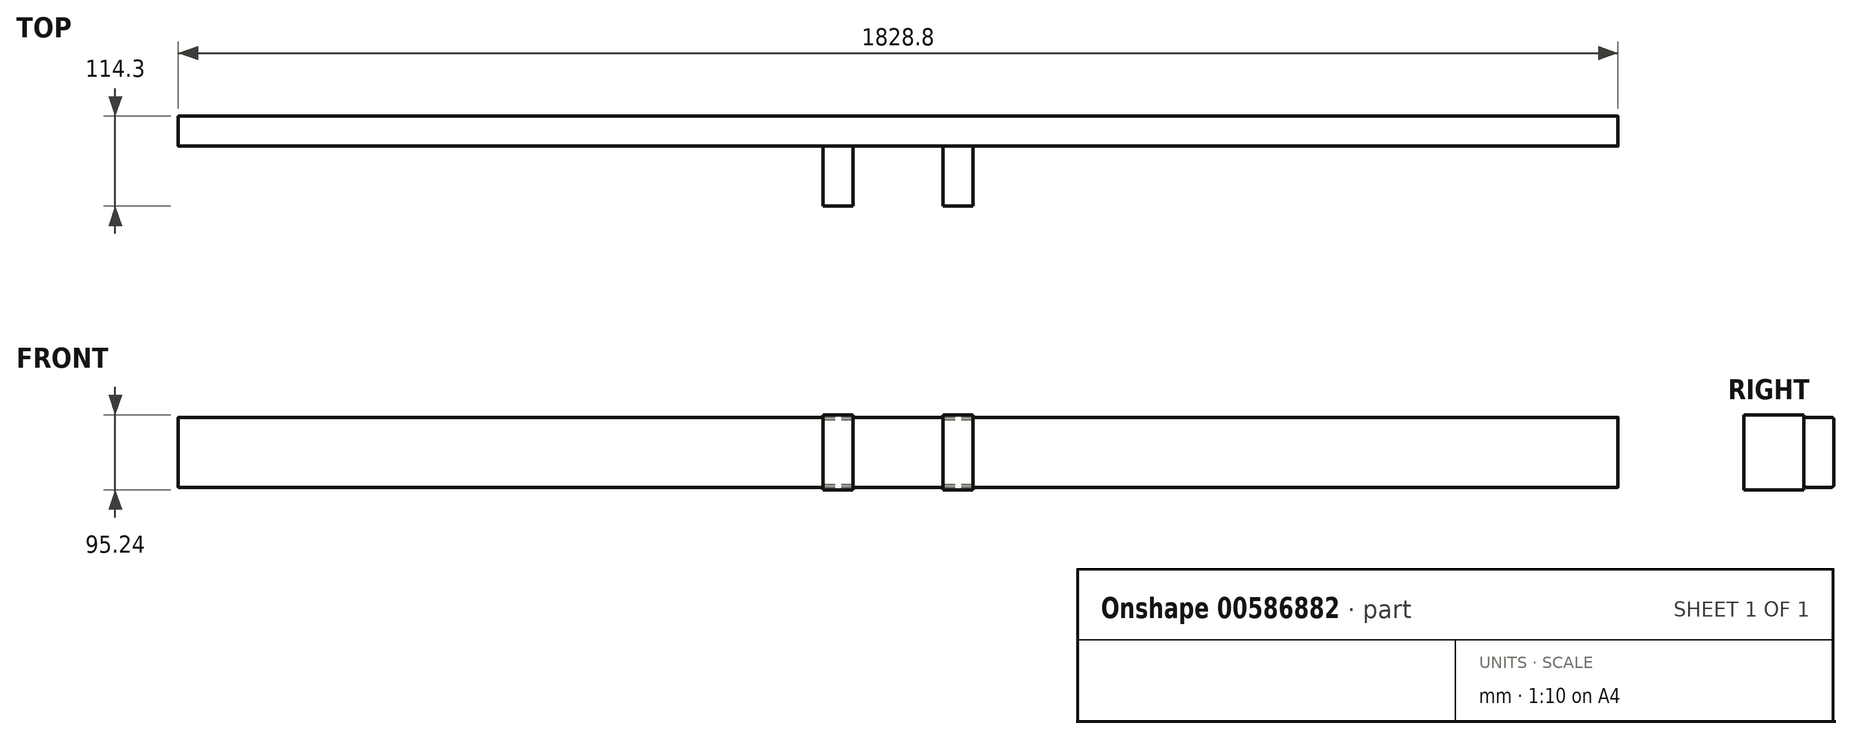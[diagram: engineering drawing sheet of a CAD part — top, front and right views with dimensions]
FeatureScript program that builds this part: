
annotation { "Feature Type Name" : "Feature", "Feature Type Description" : "" }
export const myFeature = defineFeature(function(context is Context, id is Id, definition is map)
    precondition{}
    {
        {
            var Q0;
            Q0=qCreatedBy(makeId("Right.planeOp"),FACE);
            var sketch = newSketch(context, id + "F0", { "sketchPlane" : qUnion([Q0])});
            skLineSegment(sketch, "E0.bottom", {"start": v(-19.05, 44.45) * mm, "end": v(19.05, 44.45) * mm});
            skLineSegment(sketch, "E0.top", {"start": v(-19.05, -44.45) * mm, "end": v(19.05, -44.45) * mm});
            skLineSegment(sketch, "E0.left", {"start": v(-19.05, 44.45) * mm, "end": v(-19.05, -44.45) * mm});
            skLineSegment(sketch, "E0.right", {"start": v(19.05, 44.45) * mm, "end": v(19.05, -44.45) * mm});
            skPoint(sketch, "E0.middle", {"position": v(0, 0) * mm});
            skSolve(sketch);
        }
        {
            var Q0;
            Q0 = qSketchRegion(id + "F0", true);
            extrude(context, id + "F1", {"entities" : qUnion([Q0]), "endBound" : BoundingType.SYMMETRIC, "depth" : 1828.8 * mm, "offsetDistance" : 25.4 * mm});
        }
        {
            var Q0;
            Q0=makeQuery(id+"F1.opExtrude","SWEPT_EDGE",EDGE,{"disambiguationData":[OSD([sQuery(id+"F0.wireOp",EDGE,"E0.bottom"),sQuery(id+"F0.wireOp",EDGE,"E0.left")])]});
            var Q1;
            Q1=makeQuery(id+"F1.opExtrude","SWEPT_EDGE",EDGE,{"disambiguationData":[OSD([sQuery(id+"F0.wireOp",EDGE,"E0.bottom"),sQuery(id+"F0.wireOp",EDGE,"E0.right")])]});
            var Q2;
            Q2=makeQuery(id+"F1.opExtrude","SWEPT_EDGE",EDGE,{"disambiguationData":[OSD([sQuery(id+"F0.wireOp",EDGE,"E0.top"),sQuery(id+"F0.wireOp",EDGE,"E0.left")])]});
            var Q3;
            Q3=makeQuery(id+"F1.opExtrude","SWEPT_EDGE",EDGE,{"disambiguationData":[OSD([sQuery(id+"F0.wireOp",EDGE,"E0.top"),sQuery(id+"F0.wireOp",EDGE,"E0.right")])]});
            fillet(context, id + "F2", {"entities" : qUnion([Q0, Q1, Q2, Q3]), "radius" : 3.17 * mm, "tangentPropagation" : true, "allowEdgeOverflow" : false});
        }
        {
            var Q0;
            Q0=makeQuery(id+"F1.opExtrude","SWEPT_FACE",FACE,{"disambiguationData":[OSD([sQuery(id+"F0.wireOp",EDGE,"E0.left")])]});
            var sketch = newSketch(context, id + "F3", { "sketchPlane" : qUnion([Q0])});
            skSolve(sketch);
        }
        {
            var Q0;
            {var subQ0=sQuery(id+"F0.wireOp",EDGE,"E0.left");Q0=makeQuery(id+"F3.imprint","IMPRINT",FACE,{"disambiguationData":[TD([[makeQuery(id+"F3.imprint","IMPRINT",EDGE,{"derivedFrom":makeQuery(id+"F1.opExtrude","CAP_EDGE",EDGE,{"disambiguationData":[OSD([subQ0])],"isStart":true})}),1.0]])]});}
            var sketch = newSketch(context, id + "F4", { "sketchPlane" : qUnion([Q0])});
            skLineSegment(sketch, "E1.bottom", {"start": v(57.15, 47.63) * mm, "end": v(95.25, 47.63) * mm});
            skLineSegment(sketch, "E1.top", {"start": v(57.15, -47.63) * mm, "end": v(95.25, -47.63) * mm});
            skLineSegment(sketch, "E1.left", {"start": v(57.15, 47.63) * mm, "end": v(57.15, -47.63) * mm});
            skLineSegment(sketch, "E1.right", {"start": v(95.25, 47.63) * mm, "end": v(95.25, -47.63) * mm});
            skPoint(sketch, "E1.middle", {"position": v(76.2, 0) * mm});
            skSolve(sketch);
        }
        {
            var Q0;
            Q0 = qSketchRegion(id + "F4", true);
            extrude(context, id + "F5", {"entities" : qUnion([Q0]), "depth" : 76.2 * mm, "offsetDistance" : 25.4 * mm});
        }
        {
            var Q0;
            Q0=makeQuery(id+"F5.opExtrude","SWEPT_BODY",BODY,{"disambiguationData":[OSD([sQuery(id+"F4.wireOp",EDGE,"E1.bottom"),sQuery(id+"F4.wireOp",EDGE,"E1.top"),sQuery(id+"F4.wireOp",EDGE,"E1.left"),sQuery(id+"F4.wireOp",EDGE,"E1.right")])]});
            var Q1;
            Q1=qCreatedBy(makeId("Right.planeOp"),FACE);
            mirror(context, id + "F6", {"operationType" : NewBodyOperationType.ADD, "entities" : qUnion([Q0]), "mirrorPlane" : qUnion([Q1])});
        }
    });
